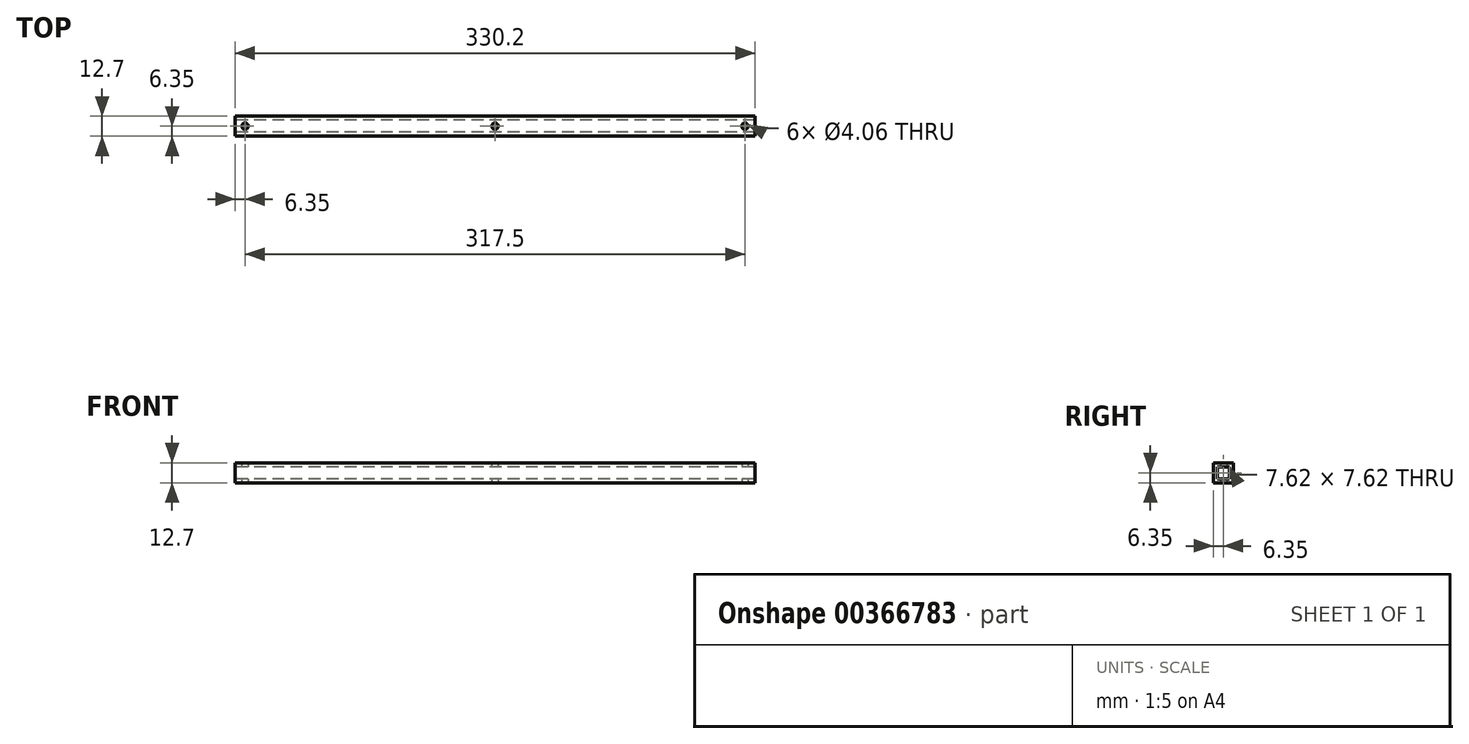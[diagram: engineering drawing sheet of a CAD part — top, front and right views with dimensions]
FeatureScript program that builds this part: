
annotation { "Feature Type Name" : "Feature", "Feature Type Description" : "" }
export const myFeature = defineFeature(function(context is Context, id is Id, definition is map)
    precondition{}
    {
        {
            var Q0;
            Q0=qCreatedBy(makeId("Top.planeOp"),FACE);
            var sketch = newSketch(context, id + "F0", { "sketchPlane" : qUnion([Q0])});
            skLineSegment(sketch, "E0.bottom", {"start": v(165.1, -6.35) * mm, "end": v(-165.1, -6.35) * mm});
            skLineSegment(sketch, "E0.top", {"start": v(165.1, 6.35) * mm, "end": v(-165.1, 6.35) * mm});
            skLineSegment(sketch, "E0.left", {"start": v(165.1, -6.35) * mm, "end": v(165.1, 6.35) * mm});
            skLineSegment(sketch, "E0.right", {"start": v(-165.1, -6.35) * mm, "end": v(-165.1, 6.35) * mm});
            skPoint(sketch, "E0.middle", {"position": v(0, 0) * mm});
            skCircle(sketch, "E1", {"center": v(0, 0) * mm, "radius": 2.03 * mm});
            skCircle(sketch, "E2", {"center": v(158.75, 0) * mm, "radius": 2.03 * mm});
            skCircle(sketch, "E3", {"center": v(-158.75, 0) * mm, "radius": 2.03 * mm});
            skSolve(sketch);
        }
        {
            var Q0;
            Q0=makeQuery(id+"F0.imprint","IMPRINT",FACE,{"disambiguationData":[TD([[makeQuery(id+"F0.imprint","IMPRINT",EDGE,{"derivedFrom":sQuery(id+"F0.wireOp",EDGE,"E0.bottom")}),-1.0]])]});
            extrude(context, id + "F1", {"entities" : qUnion([Q0]), "depth" : 12.7 * mm});
        }
        {
            var Q0;
            Q0=makeQuery(id+"F1.opExtrude","SWEPT_FACE",FACE,{"disambiguationData":[OSD([sQuery(id+"F0.wireOp",EDGE,"E0.right")])]});
            var sketch = newSketch(context, id + "F2", { "sketchPlane" : qUnion([Q0])});
            skLineSegment(sketch, "E4.bottom", {"start": v(3.8, 10.16) * mm, "end": v(-3.81, 10.16) * mm});
            skLineSegment(sketch, "E4.top", {"start": v(3.8, 2.54) * mm, "end": v(-3.81, 2.54) * mm});
            skLineSegment(sketch, "E4.left", {"start": v(3.8, 10.16) * mm, "end": v(3.8, 2.54) * mm});
            skLineSegment(sketch, "E4.right", {"start": v(-3.81, 10.16) * mm, "end": v(-3.81, 2.54) * mm});
            skSolve(sketch);
        }
        {
            var Q0;
            Q0=makeQuery(id+"F2.imprint","IMPRINT",FACE,{"disambiguationData":[TD([[makeQuery(id+"F2.imprint","IMPRINT",EDGE,{"derivedFrom":sQuery(id+"F2.wireOp",EDGE,"E4.bottom")}),1.0]])]});
            extrude(context, id + "F3", {"entities" : qUnion([Q0]), "operationType" : NewBodyOperationType.REMOVE, "oppositeDirection" : true, "depth" : 424.18 * mm});
        }
    });
